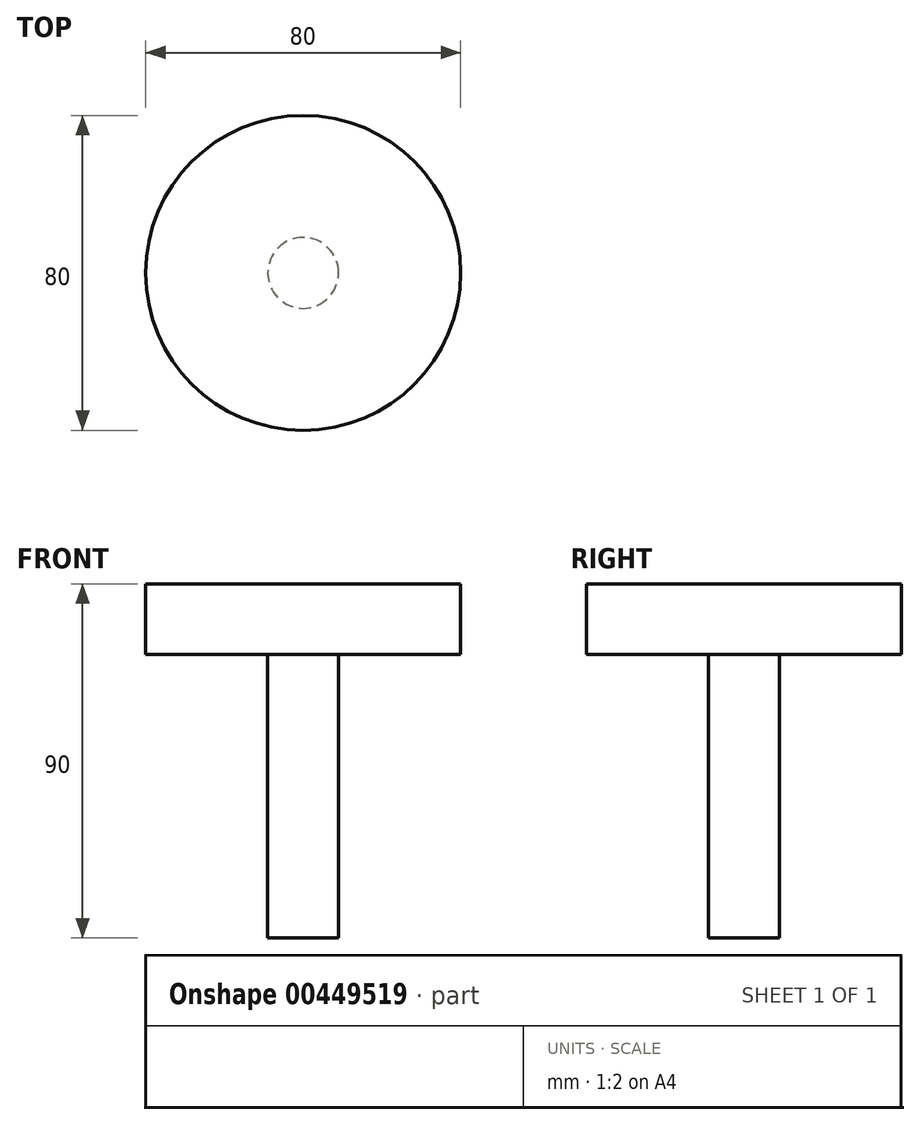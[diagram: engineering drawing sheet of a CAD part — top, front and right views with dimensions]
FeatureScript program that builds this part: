
annotation { "Feature Type Name" : "Feature", "Feature Type Description" : "" }
export const myFeature = defineFeature(function(context is Context, id is Id, definition is map)
    precondition{}
    {
        {
            var Q0;
            Q0=qCreatedBy(makeId("Front.planeOp"),FACE);
            var sketch = newSketch(context, id + "F0", { "sketchPlane" : qUnion([Q0])});
            skLineSegment(sketch, "E0", {"start": v(-40, 90) * mm, "end": v(-40, 72) * mm});
            skLineSegment(sketch, "E1", {"start": v(-40, 72) * mm, "end": v(-9, 72) * mm});
            skLineSegment(sketch, "E2", {"start": v(-9, 72) * mm, "end": v(-9, 0) * mm});
            skLineSegment(sketch, "E3.MirrorCS", {"start": v(40, 90) * mm, "end": v(40, 72) * mm});
            skLineSegment(sketch, "E4.MirrorCS", {"start": v(40, 72) * mm, "end": v(9, 72) * mm});
            skLineSegment(sketch, "E5.MirrorCS", {"start": v(9, 72) * mm, "end": v(9, 0) * mm});
            skLineSegment(sketch, "E6", {"start": v(-40, 90) * mm, "end": v(40, 90) * mm});
            skLineSegment(sketch, "E7", {"start": v(-9, 0) * mm, "end": v(9, 0) * mm});
            skLineSegment(sketch, "E8", {"start": v(0, 90) * mm, "end": v(0, 0) * mm});
            skSolve(sketch);
        }
        {
            var Q0;
            {var subQ1=sQuery(id+"F0.wireOp",EDGE,"E3.MirrorCS");Q0=makeQuery(id+"F0.imprint","IMPRINT",FACE,{"disambiguationData":[TD([[makeQuery(id+"F0.imprint","IMPRINT",EDGE,{"derivedFrom":subQ1}),-1.0]])]});}
            var Q1;
            Q1=sQuery(id+"F0.wireOp",EDGE,"E8");
            revolve(context, id + "F1", {"entities" : qUnion([Q0]), "axis" : qUnion([Q1]), "revolveType" : RevolveType.FULL});
        }
    });
